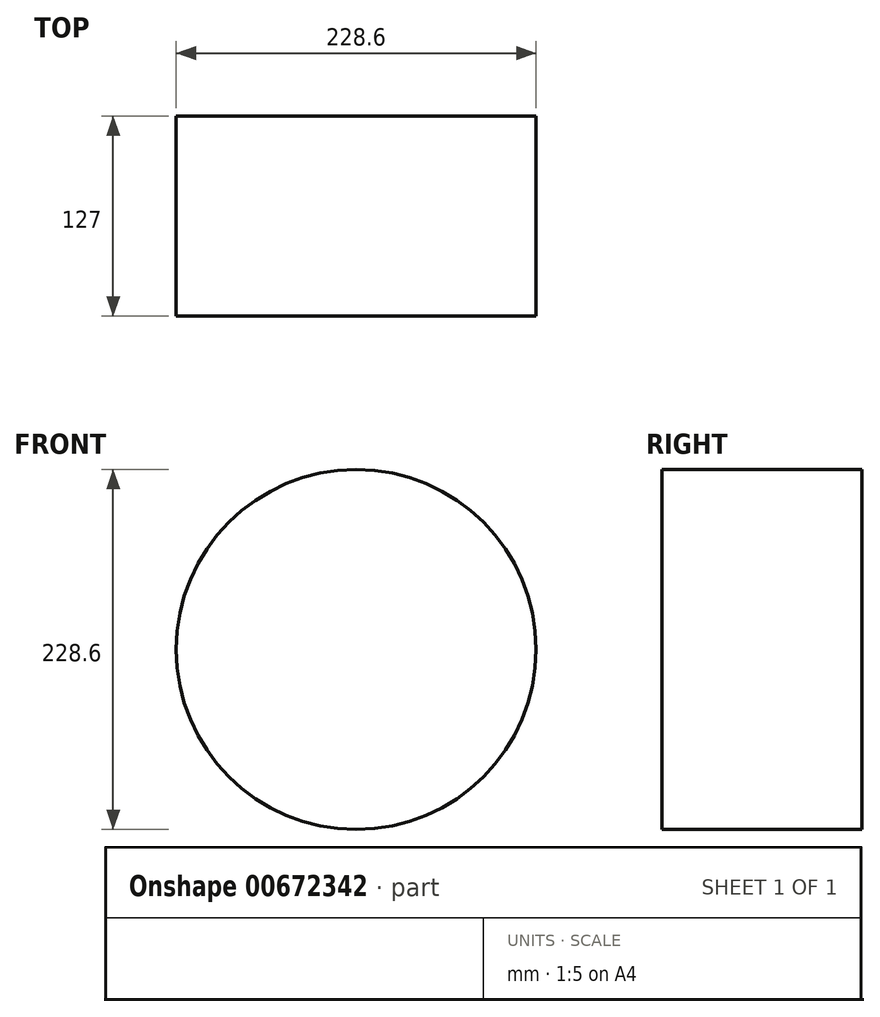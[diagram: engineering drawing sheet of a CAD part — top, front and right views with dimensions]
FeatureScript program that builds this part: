
annotation { "Feature Type Name" : "Feature", "Feature Type Description" : "" }
export const myFeature = defineFeature(function(context is Context, id is Id, definition is map)
    precondition{}
    {
        {
            var Q0;
            Q0=qCreatedBy(makeId("Front.planeOp"),FACE);
            var sketch = newSketch(context, id + "F0", { "sketchPlane" : qUnion([Q0])});
            skCircle(sketch, "E0", {"center": v(0, 0) * mm, "radius": 114.3 * mm});
            skSolve(sketch);
        }
        {
            var Q0;
            Q0=makeQuery(id+"F0.imprint","IMPRINT",FACE,{"disambiguationData":[TD([[makeQuery(id+"F0.imprint","IMPRINT",EDGE,{"derivedFrom":sQuery(id+"F0.wireOp",EDGE,"E0")}),1.0]])]});
            extrude(context, id + "F1", {"entities" : qUnion([Q0]), "endBound" : BoundingType.SYMMETRIC, "depth" : 127 * mm, "offsetDistance" : 25.4 * mm});
        }
    });
